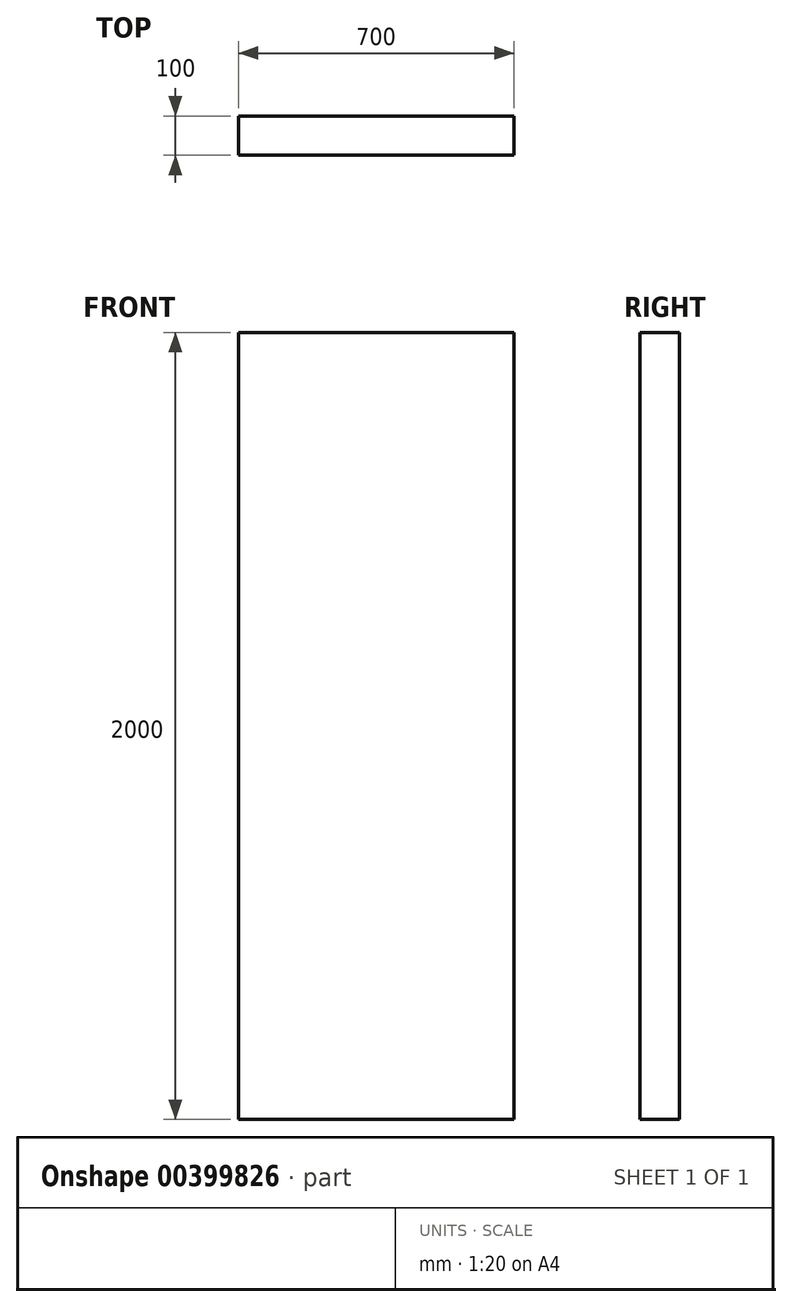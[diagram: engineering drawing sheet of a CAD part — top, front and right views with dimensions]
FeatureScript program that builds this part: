
annotation { "Feature Type Name" : "Feature", "Feature Type Description" : "" }
export const myFeature = defineFeature(function(context is Context, id is Id, definition is map)
    precondition{}
    {
        {
            var Q0;
            Q0=qCreatedBy(makeId("Front.planeOp"),FACE);
            var sketch = newSketch(context, id + "F0", { "sketchPlane" : qUnion([Q0])});
            skLineSegment(sketch, "E0.bottom", {"start": v(0, 0) * mm, "end": v(700, 0) * mm});
            skLineSegment(sketch, "E0.top", {"start": v(0, 2000) * mm, "end": v(700, 2000) * mm});
            skLineSegment(sketch, "E0.left", {"start": v(0, 0) * mm, "end": v(0, 2000) * mm});
            skLineSegment(sketch, "E0.right", {"start": v(700, 0) * mm, "end": v(700, 2000) * mm});
            skSolve(sketch);
        }
        {
            var Q0;
            Q0 = qSketchRegion(id + "F0", true);
            extrude(context, id + "F1", {"entities" : qUnion([Q0]), "depth" : 100 * mm});
        }
    });
